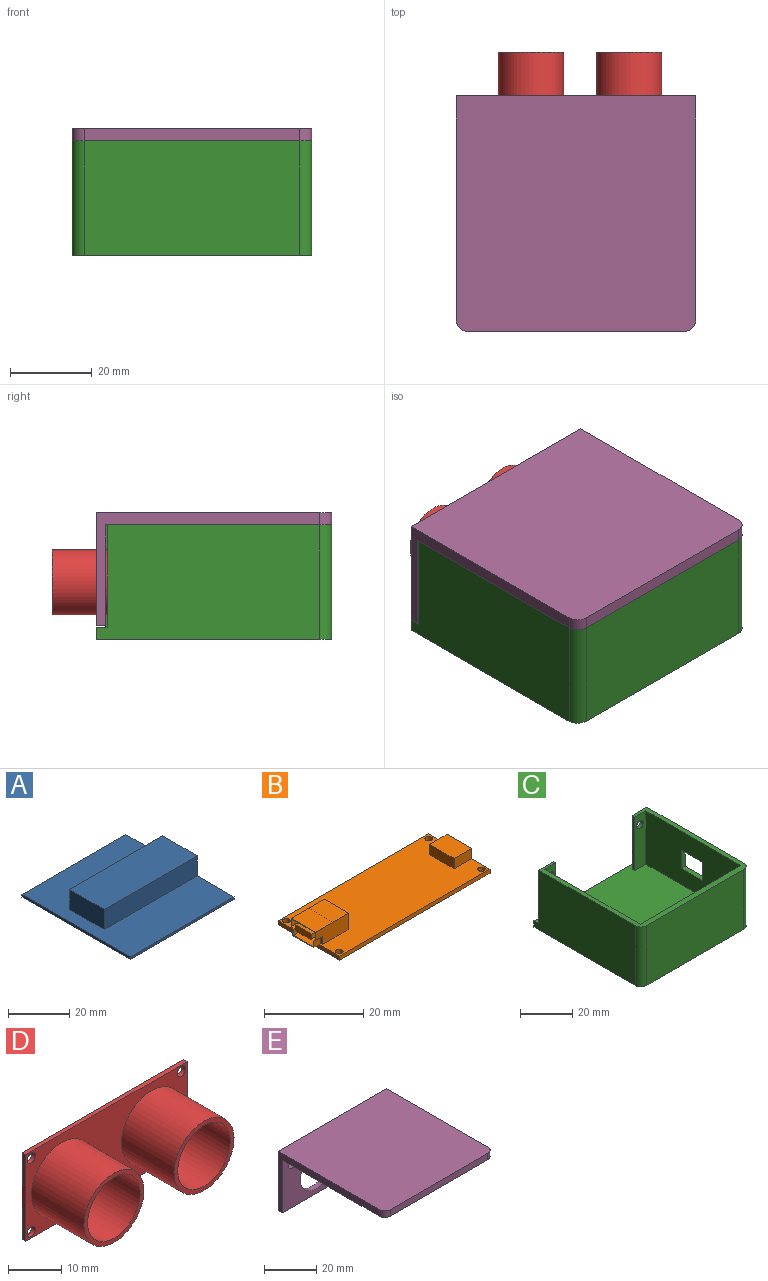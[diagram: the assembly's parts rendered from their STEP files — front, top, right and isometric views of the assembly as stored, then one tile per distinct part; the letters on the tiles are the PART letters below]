
ASSEMBLY  parts=5 mates=4
PART A: 10 faces, bbox 48x50x9 mm
  f0: plane 50x48mm, normal (0,0,1), area 1712mm2, adj f1,f2,f3,f4,f6,f7,f8
  f1: plane 48x1mm, normal (0,-1,0), area 48mm2, adj f0,f2,f4,f5
  f2: plane 50x9mm, normal (1,0,0), area 178mm2, adj f0,f1,f3,f5,f6,f8,f9
  f3: plane 48x1mm, normal (0,1,0), area 48mm2, adj f0,f2,f4,f5
  f4: plane 50x1mm, normal (-1,0,0), area 50mm2, adj f0,f1,f3,f5
  f5: plane 50x48mm, normal (0,0,-1), area 2400mm2, adj f1,f2,f3,f4
  f6: plane 43x8mm, normal (0,1,0), area 344mm2, adj f0,f2,f7,f9
  f7: plane 16x8mm, normal (-1,0,0), area 128mm2, adj f0,f6,f8,f9
  f8: plane 43x8mm, normal (0,-1,0), area 344mm2, adj f0,f2,f7,f9
  f9: plane 43x16mm, normal (0,0,1), area 688mm2, adj f2,f6,f7,f8
PART B: 42 faces, bbox 44.5x17.5x5 mm
  f0: plane 6x1.5mm, normal (0,0,-1), area 9mm2, adj f4,f12,f35,f37
  f1: plane 9.5x4mm, normal (0,1,0), area 34mm2, adj f2,f12,f14,f15,f38,f39
  f2: plane 43x17.5mm, normal (0,0,1), area 654.9mm2, adj f1,f3,f4,f5,f6,f7,f8,f9
  f3: plane 43x1mm, normal (0,1,0), area 43mm2, adj f2,f4,f9,f11
  f4: plane 17.5x1mm, normal (-1,0,0), area 17.5mm2, adj f0,f2,f3,f5,f11
  f5: plane 43x1mm, normal (0,-1,0), area 43mm2, adj f2,f4,f9,f11
  f6: cylinder r=0.75mm len=1.5mm, axis (0,0,1), area 4.7mm2, adj f2,f11
  f7: cylinder r=0.75mm len=1.5mm, axis (0,0,1), area 4.7mm2, adj f2,f11
  f8: cylinder r=0.75mm len=1.5mm, axis (0,0,1), area 4.7mm2, adj f2,f11
  f9: plane 17.5x3.5mm, normal (1,0,0), area 35mm2, adj f2,f3,f5,f11,f16,f18,f19
  f10: cylinder r=0.75mm len=1.5mm, axis (0,0,1), area 4.7mm2, adj f2,f11
  f11: plane 43x17.5mm, normal (0,0,-1), area 745.4mm2, adj f3,f4,f5,f6,f7,f8,f9,f10
  f12: plane 7x4mm, normal (-1,0,0), area 2.1mm2, adj f0,f1,f13,f15,f20,f21,f22,f23
  f13: plane 9.5x4mm, normal (0,-1,0), area 34mm2, adj f2,f12,f14,f15,f34,f36
  f14: plane 7x4mm, normal (1,0,0), area 28mm2, adj f1,f2,f13,f15
  f15: plane 9.5x7mm, normal (0,0,1), area 66.5mm2, adj f1,f12,f13,f14
  f16: plane 5x2.5mm, normal (0,1,0), area 12.5mm2, adj f2,f9,f17,f19
  f17: plane 7x2.5mm, normal (-1,0,0), area 17.5mm2, adj f2,f16,f18,f19
  f18: plane 5x2.5mm, normal (0,-1,0), area 12.5mm2, adj f2,f9,f17,f19
  f19: plane 7x5mm, normal (0,0,1), area 35mm2, adj f9,f16,f17,f18
  f20: plane 5.8x5mm, normal (0,0,1), area 29mm2, adj f12,f21,f31,f32
  f21: plane 5x1.44mm, normal (0,1,0), area 7.2mm2, adj f12,f20,f22,f32
  f22: plane 5x0.5mm, normal (0,0.71,0.71), area 3.5mm2, adj f12,f21,f23,f32
  f23: plane 5x1.86mm, normal (0,1,0), area 9.3mm2, adj f12,f22,f24,f32
  f24: plane 6.8x5mm, normal (0,0,-1), area 34mm2, adj f12,f23,f25,f32
  f25: plane 5x1.86mm, normal (0,-1,0), area 9.3mm2, adj f12,f24,f26,f32
  f26: plane 5x0.5mm, normal (0,-0.71,0.71), area 3.5mm2, adj f12,f25,f31,f32
  f27: plane 5x3.98mm, normal (0,0,-1), area 19.9mm2, adj f32,f33,f40,f41
  f28: plane 5x1.1mm, normal (0,1,0), area 5.5mm2, adj f29,f32,f33,f40
  f29: plane 5x4.78mm, normal (0,0,1), area 23.9mm2, adj f28,f30,f32,f33
  f30: plane 5x1.1mm, normal (0,-1,0), area 5.5mm2, adj f29,f32,f33,f41
  f31: plane 5x1.44mm, normal (0,-1,0), area 7.2mm2, adj f12,f20,f26,f32
  f32: plane 6.8x3.8mm, normal (-1,0,0), area 17.1mm2, adj f20,f21,f22,f23,f24,f25,f26,f27
  f33: plane 4.78x1.5mm, normal (-1,0,0), area 7mm2, adj f27,f28,f29,f30,f40,f41
  f34: plane 2x0.5mm, normal (0,-0.71,-0.71), area 1.4mm2, adj f12,f13,f35,f36
  f35: plane 2x1.5mm, normal (0,-1,0), area 3mm2, adj f0,f2,f12,f34,f36
  f36: plane 2x0.5mm, normal (-1,0,0), area 0.9mm2, adj f2,f13,f34,f35
  f37: plane 2x1.5mm, normal (0,1,0), area 3mm2, adj f0,f2,f12,f38,f39
  f38: plane 2x0.5mm, normal (0,0.71,-0.71), area 1.4mm2, adj f1,f12,f37,f39
  f39: plane 2x0.5mm, normal (-1,0,0), area 0.9mm2, adj f1,f2,f37,f38
  f40: plane 5x0.4mm, normal (0,0.71,-0.71), area 2.8mm2, adj f27,f28,f32,f33
  f41: plane 5x0.4mm, normal (0,-0.71,-0.71), area 2.8mm2, adj f27,f30,f32,f33
PART C: 24 faces, bbox 58.6x57.6x28 mm
  f0: plane 54.6x28mm, normal (1,0,0), area 1371.5mm2, adj f2,f4,f6,f7,f15,f16,f17,f18
  f1: plane 51.1x25mm, normal (-1,0,0), area 1178.6mm2, adj f2,f9,f10,f15,f16,f17,f18,f19
  f2: plane 58.6x55.27mm, normal (0,0,1), area 3002.5mm2, adj f0,f1,f4,f5,f7,f8,f9,f10
  f3: plane 52.6x28mm, normal (0,-1,0), area 1472.8mm2, adj f6,f15,f22,f23
  f4: plane 58.6x3mm, normal (0,1,0), area 175.8mm2, adj f0,f2,f5,f6
  f5: plane 54.6x28mm, normal (-1,0,0), area 1462.2mm2, adj f2,f4,f6,f14,f15,f23
  f6: plane 58.6x57.6mm, normal (0,0,-1), area 3371.5mm2, adj f0,f3,f4,f5,f22,f23
  f7: plane 25x8mm, normal (0,1,0), area 190.4mm2, adj f0,f2,f8,f15,f21
  f8: plane 25x1.5mm, normal (-1,0,0), area 37.5mm2, adj f2,f7,f9,f15
  f9: plane 25x6mm, normal (0,-1,0), area 140.4mm2, adj f1,f2,f8,f15,f21
  f10: plane 54.6x25mm, normal (-0.01,1,0), area 1365mm2, adj f1,f2,f11,f15
  f11: plane 51.43x25mm, normal (1,0,0), area 1285.8mm2, adj f2,f10,f12,f15
  f12: plane 25x6mm, normal (0,-1,0), area 140.4mm2, adj f2,f11,f13,f15,f20
  f13: plane 25x1.17mm, normal (1,0,0), area 29.2mm2, adj f2,f12,f14,f15
  f14: plane 25x8mm, normal (0,1,0), area 190.4mm2, adj f2,f5,f13,f15,f20
  f15: plane 58.6x55.27mm, normal (0,0,1), area 369mm2, adj f0,f1,f3,f5,f7,f8,f9,f10
  f16: plane 11.5x2mm, normal (0,0,1), area 23mm2, adj f0,f1,f17,f19
  f17: plane 8.6x2mm, normal (0,-1,0), area 17.2mm2, adj f0,f1,f16,f18
  f18: plane 11.5x2mm, normal (0,0,-1), area 23mm2, adj f0,f1,f17,f19
  f19: plane 8.6x2mm, normal (0,1,0), area 17.2mm2, adj f0,f1,f16,f18
  f20: cylinder r=1.75mm len=3.5mm, axis (0,1,0), area 12.9mm2, adj f12,f14
  f21: cylinder r=1.75mm len=3.5mm, axis (0,1,0), area 16.5mm2, adj f7,f9
  f22: cylinder r=3mm len=28mm, axis (0,0,1), area 131.9mm2, adj f0,f3,f6,f15
  f23: cylinder r=3mm len=28mm, axis (0,0,-1), area 131.9mm2, adj f3,f5,f6,f15
PART D: 18 faces, bbox 43x15x20 mm
  f0: plane 43x1mm, normal (0,0,1), area 43mm2, adj f1,f3,f4,f5
  f1: plane 20x1mm, normal (-1,0,0), area 20mm2, adj f0,f2,f4,f5
  f2: plane 43x1mm, normal (0,0,-1), area 43mm2, adj f1,f3,f4,f5
  f3: plane 20x1mm, normal (1,0,0), area 20mm2, adj f0,f2,f4,f5
  f4: plane 43x20mm, normal (0,-1,0), area 441.3mm2, adj f0,f1,f2,f3,f6,f7,f8,f9
  f5: plane 43x20mm, normal (0,1,0), area 843.4mm2, adj f0,f1,f2,f3,f6,f7,f8,f9
  f6: cylinder r=1.15mm len=2.3mm, axis (0,-1,0), area 7.2mm2, adj f4,f5
  f7: cylinder r=1.15mm len=2.3mm, axis (0,-1,0), area 7.2mm2, adj f4,f5
  f8: cylinder r=1.15mm len=2.3mm, axis (0,-1,0), area 7.2mm2, adj f4,f5
  f9: cylinder r=1.15mm len=2.3mm, axis (0,-1,0), area 7.2mm2, adj f4,f5
  f10: cylinder r=7mm len=14mm, axis (0,1,0), area 615.8mm2, adj f12,f13
  f11: cylinder r=8mm len=16mm, axis (0,1,0), area 703.7mm2, adj f4,f12
  f12: plane 16x16mm, normal (0,-1,0), area 47.1mm2, adj f10,f11
  f13: plane 14x14mm, normal (0,-1,0), area 153.9mm2, adj f10
  f14: cylinder r=7mm len=14mm, axis (0,1,0), area 615.8mm2, adj f16,f17
  f15: cylinder r=8mm len=16mm, axis (0,1,0), area 703.7mm2, adj f4,f16
  f16: plane 16x16mm, normal (0,-1,0), area 47.1mm2, adj f14,f15
  f17: plane 14x14mm, normal (0,-1,0), area 153.9mm2, adj f14
PART E: 14 faces, bbox 58.6x57.6x27.7 mm
  f0: plane 54.6x27.7mm, normal (1,0,0), area 220.6mm2, adj f1,f4,f5,f6,f7,f13
  f1: plane 58.6x27.7mm, normal (0,1,0), area 1150mm2, adj f0,f2,f4,f7,f8,f9,f10,f11
  f2: plane 54.6x27.7mm, normal (-1,0,0), area 220.6mm2, adj f1,f4,f5,f6,f7,f12
  f3: plane 52.6x3mm, normal (0,-1,0), area 157.8mm2, adj f4,f5,f12,f13
  f4: plane 58.6x57.6mm, normal (0,0,1), area 3371.5mm2, adj f0,f1,f2,f3,f12,f13
  f5: plane 58.6x55.3mm, normal (0,0,-1), area 3236.7mm2, adj f0,f2,f3,f6,f12,f13
  f6: plane 58.6x24.7mm, normal (0,-1,0), area 974.2mm2, adj f0,f2,f5,f7,f8,f9,f10,f11
  f7: plane 58.6x2.3mm, normal (0,0,-1), area 134.8mm2, adj f0,f1,f2,f6
  f8: cylinder r=8.5mm len=17mm, axis (0,1,0), area 122.8mm2, adj f1,f6
  f9: cylinder r=8.5mm len=17mm, axis (0,1,0), area 122.8mm2, adj f1,f6
  f10: cylinder r=1.75mm len=3.5mm, axis (0,1,0), area 25.3mm2, adj f1,f6
  f11: cylinder r=1.75mm len=3.5mm, axis (0,1,0), area 25.3mm2, adj f1,f6
  f12: cylinder r=3mm len=3mm, axis (0,0,1), area 14.1mm2, adj f2,f3,f4,f5
  f13: cylinder r=3mm len=3mm, axis (0,0,-1), area 14.1mm2, adj f0,f3,f4,f5
PLACE A t=(-13.71,27.02,-13.02)mm
PLACE B rot(axis=(0,0,1),180deg) t=(-11.21,27.02,-3.02)mm
PLACE C t=(-13.71,27.02,-16.02)mm
PLACE D rot(axis=(0,0,1),180deg) t=(-13.71,51.52,-2.02)mm
PLACE E t=(-14.71,27.02,11.98)mm
MATE parallel C.f2 <-> A.f5  axis (0,0,1) through (-14.76,28.23,-13.02)mm
MATE parallel E.f5 <-> C.f15  axis (0,0,-1) through (-14.71,-1.78,11.98)mm
MATE parallel D.f2 <-> A.f0  axis (0,0,-1) through (-13.71,52.02,-12.02)mm
MATE parallel B.f11 <-> A.f9  axis (0,0,-1) through (-11.21,27.02,-4.02)mm
